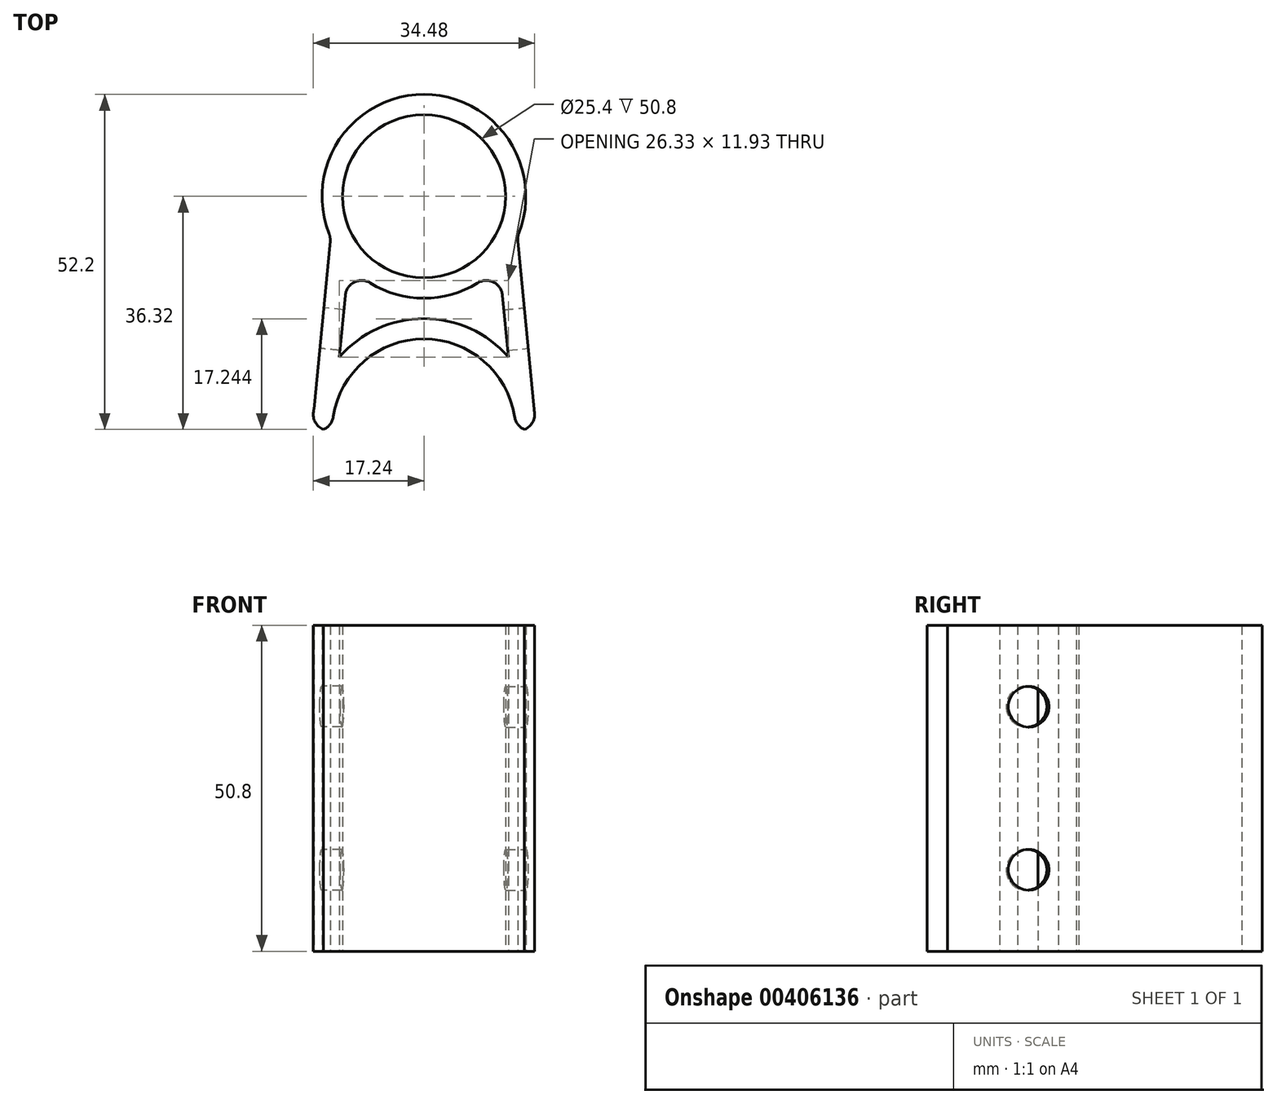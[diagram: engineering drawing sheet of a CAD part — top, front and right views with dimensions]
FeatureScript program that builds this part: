
annotation { "Feature Type Name" : "Feature", "Feature Type Description" : "" }
export const myFeature = defineFeature(function(context is Context, id is Id, definition is map)
    precondition{}
    {
        {
            var Q0;
            Q0=qCreatedBy(makeId("Top.planeOp"),FACE);
            var sketch = newSketch(context, id + "F0", { "sketchPlane" : qUnion([Q0])});
            skCircle(sketch, "E0", {"center": v(0, 0) * mm, "radius": 12.7 * mm});
            skCircle(sketch, "E1", {"center": v(0, 0) * mm, "radius": 15.88 * mm});
            skCircle(sketch, "E2", {"center": v(0, -36.51) * mm, "radius": 14.29 * mm});
            skLineSegment(sketch, "E3", {"start": v(58.17, -36.51) * mm, "end": v(-68.84, -36.51) * mm, "construction": true});
            skLineSegment(sketch, "E4", {"start": v(58.57, -6.35) * mm, "end": v(-59.78, -6.35) * mm, "construction": true});
            skPoint(sketch, "E5.orphan", {"position": v(0, -6.35) * mm});
            skLineSegment(sketch, "E6", {"start": v(-14.55, -6.35) * mm, "end": v(-17.46, -36.51) * mm});
            skLineSegment(sketch, "E7.MirrorCS", {"start": v(14.55, -6.35) * mm, "end": v(17.46, -36.51) * mm});
            skLineSegment(sketch, "E8", {"start": v(0, -36.51) * mm, "end": v(0, -19.05) * mm, "construction": true});
            skArc(sketch, "E9", {"start": v(17.46, -36.51) * mm, "mid": v(0, -19.05) * mm, "end": v(-17.46, -36.51) * mm});
            skLineSegment(sketch, "E10", {"start": v(-14.29, -36.51) * mm, "end": v(-17.46, -36.51) * mm});
            skLineSegment(sketch, "E11", {"start": v(14.29, -36.51) * mm, "end": v(17.46, -36.51) * mm});
            skLineSegment(sketch, "E12", {"start": v(-11.77, -10.65) * mm, "end": v(-13.16, -25.04) * mm});
            skLineSegment(sketch, "E13.MirrorCS", {"start": v(11.77, -10.65) * mm, "end": v(13.16, -25.04) * mm});
            skSolve(sketch);
        }
        {
            var Q0;
            {var subQ0=sQuery(id+"F0.wireOp",EDGE,"E9");var subQ1=sQuery(id+"F0.wireOp",EDGE,"E6");var subQ3=makeQuery(id+"F0.imprint","INTERSECT",VERTEX,{"derivedFrom":[subQ1,subQ0]});Q0=makeQuery(id+"F0.imprint","IMPRINT",FACE,{"disambiguationData":[TD([[makeQuery(id+"F0.imprint","IMPRINT",EDGE,{"disambiguationData":[TD([[subQ3,-1.0]])],"derivedFrom":subQ1}),-1.0]])]});}
            var Q1;
            {var subQ0=sQuery(id+"F0.wireOp",EDGE,"E9");var subQ1=sQuery(id+"F0.wireOp",EDGE,"E7.MirrorCS");var subQ3=makeQuery(id+"F0.imprint","INTERSECT",VERTEX,{"derivedFrom":[subQ1,subQ0]});Q1=makeQuery(id+"F0.imprint","IMPRINT",FACE,{"disambiguationData":[TD([[makeQuery(id+"F0.imprint","IMPRINT",EDGE,{"disambiguationData":[TD([[subQ3,-1.0]])],"derivedFrom":subQ1}),1.0]])]});}
            var Q2;
            {var subQ3=sQuery(id+"F0.wireOp",EDGE,"E12");Q2=makeQuery(id+"F0.imprint","IMPRINT",FACE,{"disambiguationData":[TD([[makeQuery(id+"F0.imprint","IMPRINT",EDGE,{"derivedFrom":subQ3}),-1.0]])]});}
            var Q3;
            {var subQ3=sQuery(id+"F0.wireOp",EDGE,"E13.MirrorCS");Q3=makeQuery(id+"F0.imprint","IMPRINT",FACE,{"disambiguationData":[TD([[makeQuery(id+"F0.imprint","IMPRINT",EDGE,{"derivedFrom":subQ3}),1.0]])]});}
            var Q4;
            Q4=makeQuery(id+"F0.imprint","IMPRINT",FACE,{"disambiguationData":[TD([[makeQuery(id+"F0.imprint","IMPRINT",EDGE,{"derivedFrom":sQuery(id+"F0.wireOp",EDGE,"E0")}),-1.0]])]});
            var Q5;
            {var subQ4=sQuery(id+"F0.wireOp",EDGE,"E10");Q5=makeQuery(id+"F0.imprint","IMPRINT",FACE,{"disambiguationData":[TD([[makeQuery(id+"F0.imprint","IMPRINT",EDGE,{"derivedFrom":subQ4}),-1.0]])]});}
            extrude(context, id + "F1", {"entities" : qUnion([Q0, Q1, Q2, Q3, Q4, Q5]), "depth" : 50.8 * mm});
        }
        {
            var Q0;
            Q0=makeQuery(id+"F1.opExtrude","SWEPT_FACE",FACE,{"disambiguationData":[OSD([sQuery(id+"F0.wireOp",EDGE,"E6")])]});
            var sketch = newSketch(context, id + "F2", { "sketchPlane" : qUnion([Q0])});
            skCircle(sketch, "E14", {"center": v(21.96, 12.68) * mm, "radius": 3.18 * mm});
            skCircle(sketch, "E15", {"center": v(21.96, 38.12) * mm, "radius": 3.18 * mm});
            skSolve(sketch);
        }
        {
            var Q0;
            Q0=makeQuery(id+"F2.imprint","IMPRINT",FACE,{"disambiguationData":[TD([[makeQuery(id+"F2.imprint","IMPRINT",EDGE,{"derivedFrom":sQuery(id+"F2.wireOp",EDGE,"E15")}),1.0]])]});
            var Q1;
            Q1=makeQuery(id+"F2.imprint","IMPRINT",FACE,{"disambiguationData":[TD([[makeQuery(id+"F2.imprint","IMPRINT",EDGE,{"derivedFrom":sQuery(id+"F2.wireOp",EDGE,"E14")}),1.0]])]});
            var Q2;
            Q2=makeQuery(id+"F1.opExtrude","SWEPT_FACE",FACE,{"disambiguationData":[OSD([sQuery(id+"F0.wireOp",EDGE,"E12")])]});
            extrude(context, id + "F3", {"entities" : qUnion([Q0, Q1]), "operationType" : NewBodyOperationType.REMOVE, "endBound" : BoundingType.UP_TO_SURFACE, "oppositeDirection" : true, "endBoundEntityFace" : qUnion([Q2]), "depth" : 12.7 * mm});
        }
        {
            var Q0;
            Q0=makeQuery(id+"F1.opExtrude","SWEPT_FACE",FACE,{"disambiguationData":[OSD([sQuery(id+"F0.wireOp",EDGE,"E7.MirrorCS")])]});
            var sketch = newSketch(context, id + "F4", { "sketchPlane" : qUnion([Q0])});
            skCircle(sketch, "E16", {"center": v(-21.96, 38.1) * mm, "radius": 3.17 * mm});
            skCircle(sketch, "E17", {"center": v(-21.96, 12.7) * mm, "radius": 3.18 * mm});
            skSolve(sketch);
        }
        {
            var Q0;
            Q0=makeQuery(id+"F4.imprint","IMPRINT",FACE,{"disambiguationData":[TD([[makeQuery(id+"F4.imprint","IMPRINT",EDGE,{"derivedFrom":sQuery(id+"F4.wireOp",EDGE,"E17")}),1.0]])]});
            var Q1;
            Q1=makeQuery(id+"F4.imprint","IMPRINT",FACE,{"disambiguationData":[TD([[makeQuery(id+"F4.imprint","IMPRINT",EDGE,{"derivedFrom":sQuery(id+"F4.wireOp",EDGE,"E16")}),1.0]])]});
            var Q2;
            Q2=makeQuery(id+"F1.opExtrude","SWEPT_FACE",FACE,{"disambiguationData":[OSD([sQuery(id+"F0.wireOp",EDGE,"E13.MirrorCS")])]});
            extrude(context, id + "F5", {"entities" : qUnion([Q0, Q1]), "operationType" : NewBodyOperationType.REMOVE, "endBound" : BoundingType.UP_TO_SURFACE, "oppositeDirection" : true, "endBoundEntityFace" : qUnion([Q2]), "depth" : 25.4 * mm});
        }
        {
            var Q0;
            Q0=makeQuery(id+"F1.opExtrude","SWEPT_EDGE",EDGE,{"disambiguationData":[OSD([sQuery(id+"F0.wireOp",EDGE,"E6"),sQuery(id+"F0.wireOp",EDGE,"E9"),sQuery(id+"F0.wireOp",EDGE,"E10")])]});
            var Q1;
            Q1=makeQuery(id+"F1.opExtrude","SWEPT_EDGE",EDGE,{"disambiguationData":[OSD([sQuery(id+"F0.wireOp",EDGE,"E7.MirrorCS"),sQuery(id+"F0.wireOp",EDGE,"E9"),sQuery(id+"F0.wireOp",EDGE,"E11")])]});
            var Q2;
            Q2=makeQuery(id+"F5.boolean.opBoolean","COPY",EDGE,{"derivedFrom":makeQuery(id+"F5.opExtrude","CAP_EDGE",EDGE,{"disambiguationData":[OSD([sQuery(id+"F4.wireOp",EDGE,"E16")])],"isStart":true})});
            var Q3;
            Q3=makeQuery(id+"F5.boolean.opBoolean","COPY",EDGE,{"derivedFrom":makeQuery(id+"F5.opExtrude","CAP_EDGE",EDGE,{"disambiguationData":[OSD([sQuery(id+"F4.wireOp",EDGE,"E17")])],"isStart":true})});
            var Q4;
            Q4=makeQuery(id+"F3.boolean.opBoolean","COPY",EDGE,{"derivedFrom":makeQuery(id+"F3.opExtrude","CAP_EDGE",EDGE,{"disambiguationData":[OSD([sQuery(id+"F2.wireOp",EDGE,"E14")])],"isStart":true})});
            var Q5;
            Q5=makeQuery(id+"F3.boolean.opBoolean","COPY",EDGE,{"derivedFrom":makeQuery(id+"F3.opExtrude","CAP_EDGE",EDGE,{"disambiguationData":[OSD([sQuery(id+"F2.wireOp",EDGE,"E15")])],"isStart":true})});
            var Q6;
            Q6=makeQuery(id+"F1.opExtrude","SWEPT_EDGE",EDGE,{"disambiguationData":[OSD([sQuery(id+"F0.wireOp",EDGE,"E1"),sQuery(id+"F0.wireOp",EDGE,"E6")])]});
            var Q7;
            Q7=makeQuery(id+"F1.opExtrude","SWEPT_EDGE",EDGE,{"disambiguationData":[OSD([sQuery(id+"F0.wireOp",EDGE,"E1"),sQuery(id+"F0.wireOp",EDGE,"E7.MirrorCS")])]});
            var Q8;
            Q8=makeQuery(id+"F1.opExtrude","SWEPT_EDGE",EDGE,{"disambiguationData":[OSD([sQuery(id+"F0.wireOp",EDGE,"E1"),sQuery(id+"F0.wireOp",EDGE,"E13.MirrorCS")])]});
            var Q9;
            Q9=makeQuery(id+"F1.opExtrude","SWEPT_EDGE",EDGE,{"disambiguationData":[OSD([sQuery(id+"F0.wireOp",EDGE,"E1"),sQuery(id+"F0.wireOp",EDGE,"E12")])]});
            var Q10;
            Q10=makeQuery(id+"F1.opExtrude","SWEPT_EDGE",EDGE,{"disambiguationData":[OSD([sQuery(id+"F0.wireOp",EDGE,"E2"),sQuery(id+"F0.wireOp",EDGE,"E11")])]});
            var Q11;
            Q11=makeQuery(id+"F1.opExtrude","SWEPT_EDGE",EDGE,{"disambiguationData":[OSD([sQuery(id+"F0.wireOp",EDGE,"E2"),sQuery(id+"F0.wireOp",EDGE,"E10")])]});
            fillet(context, id + "F6", {"entities" : qUnion([Q0, Q1, Q2, Q3, Q4, Q5, Q6, Q7, Q8, Q9, Q10, Q11]), "radius" : 2.54 * mm, "allowEdgeOverflow" : false});
        }
    });
